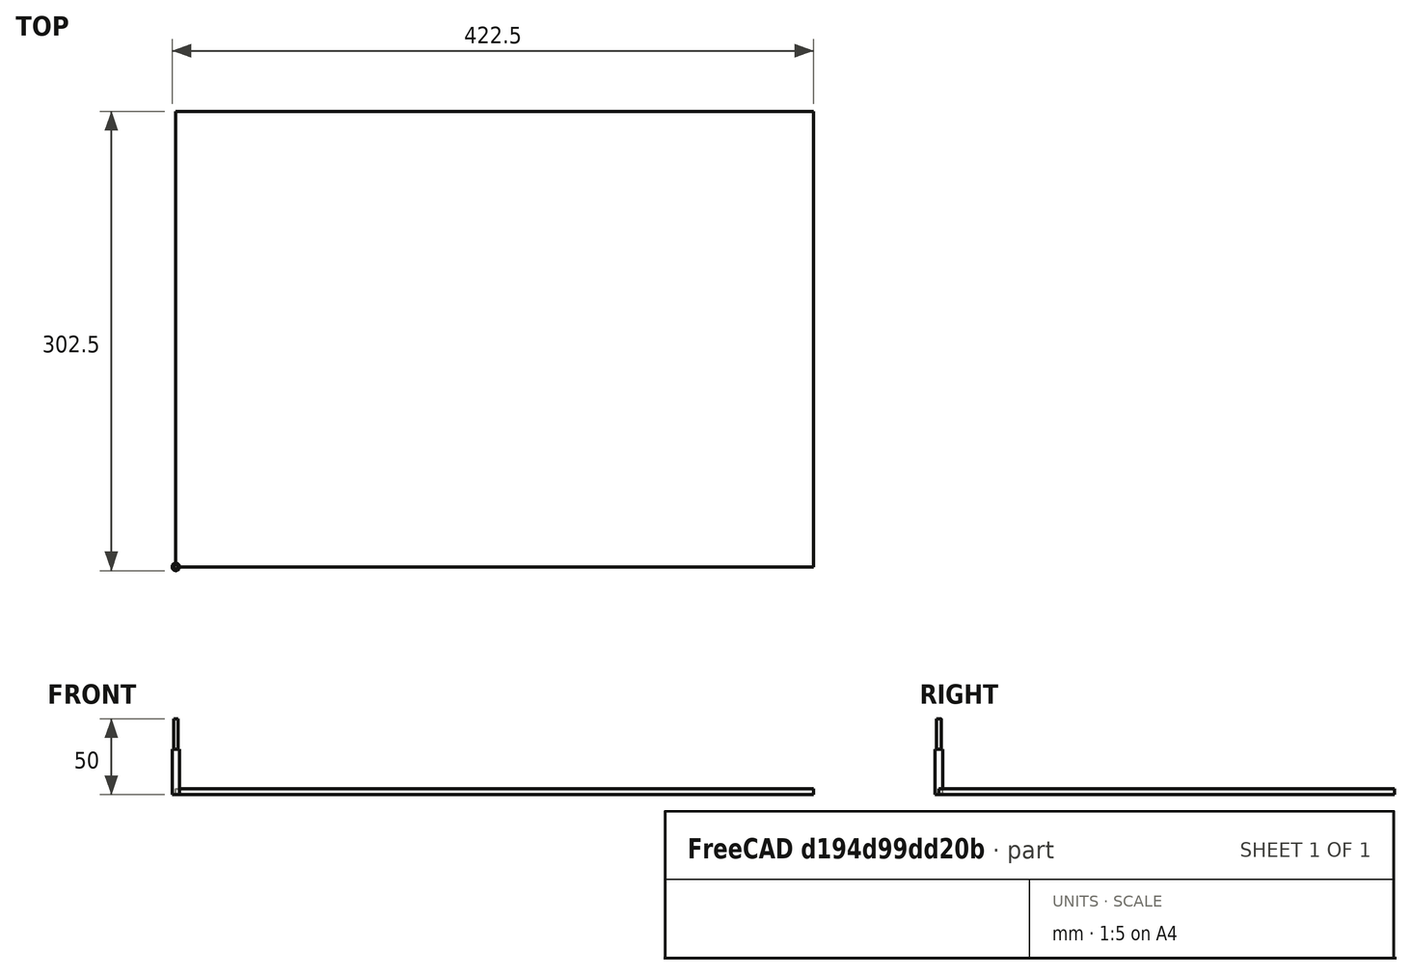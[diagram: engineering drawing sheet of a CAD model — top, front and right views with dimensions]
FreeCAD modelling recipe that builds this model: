
FCSTD DOCUMENT  (FreeCAD 0.21R33771 (Git))
Label: HousingAtari_T01
License: All rights reserved
LicenseURL: https://en.wikipedia.org/wiki/All_rights_reserved
objects: Sketcher::SketchObject×7, Part::Part2DObjectPython×5, TechDraw::DrawViewDraft×4, Path::FeaturePython×3, App::DocumentObjectGroup×3, Part::FeaturePython×2, PartDesign::Body×1, App::FeaturePython×1, Mesh::FeaturePython×1, TechDraw::DrawSVGTemplate×1, TechDraw::DrawPage×1
note: 15 computed .brp shape members not serialized (recipe doc carries the construction recipe); baked Part::Feature solids carry a one-line shape summary decoded from their .brp

FEATURE [Sketcher::SketchObject] Sketch  label="A3"
  FullyConstrained = true
  MapMode = 5
  sketch-geometry (6):
    g0: LineSegment StartX=0 StartY=0 StartZ=0 EndX=420 EndY=0 EndZ=0
    g1: LineSegment StartX=420 StartY=0 StartZ=0 EndX=420 EndY=297 EndZ=0
    g2: LineSegment StartX=0 StartY=297 StartZ=0 EndX=0 EndY=0 EndZ=0
    g3: LineSegment StartX=0 StartY=297 StartZ=0 EndX=210 EndY=297 EndZ=0
    g4: LineSegment StartX=210 StartY=297 StartZ=0 EndX=420 EndY=297 EndZ=0
    g5: LineSegment StartX=210 StartY=297 StartZ=0 EndX=210 EndY=0 EndZ=0
  constraints (16):
    c: Coincident(g0,g1)
    c: Coincident(g2,g0)
    c: Horizontal(g0)
    c: Vertical(g1)
    c: Vertical(g2)
    c: Coincident(g0,g-1)
    c: DistanceX(g2,g1) = 420
    c: DistanceY(g2,g2) = 297
    c: Coincident(g3,g2)
    c: Horizontal(g3)
    c: Coincident(g4,g3)
    c: Coincident(g4,g1)
    c: Horizontal(g4)
    c: Equal(g4,g3)
    c: Coincident(g5,g3)
    c: Symmetric(g0,g0,g5)
FEATURE [Sketcher::SketchObject] Sketch001  label="BOX-OUTLINE"
  FullyConstrained = true
  MapMode = 5
  sketch-geometry (59):
    g0: LineSegment StartX=45 StartY=255 StartZ=0 EndX=45 EndY=220 EndZ=0
    g1: LineSegment StartX=45 StartY=220 StartZ=0 EndX=45 EndY=185 EndZ=0
    g2: LineSegment StartX=45 StartY=185 StartZ=0 EndX=110 EndY=185 EndZ=0
    g3: LineSegment StartX=110 StartY=185 StartZ=0 EndX=175 EndY=185 EndZ=0
    g4: LineSegment StartX=175 StartY=185 StartZ=0 EndX=175 EndY=220 EndZ=0
    g5: LineSegment StartX=175 StartY=220 StartZ=0 EndX=175 EndY=255 EndZ=0
    g6: LineSegment StartX=175 StartY=255 StartZ=0 EndX=110 EndY=255 EndZ=0
    g7: LineSegment StartX=110 StartY=255 StartZ=0 EndX=45 EndY=255 EndZ=0
    g8: LineSegment StartX=45 StartY=185 StartZ=0 EndX=0 EndY=0 EndZ=0
    g9: LineSegment StartX=45 StartY=185 StartZ=0 EndX=45 EndY=181 EndZ=0
    g10: LineSegment StartX=45 StartY=181 StartZ=0 EndX=175 EndY=181 EndZ=0
    g11: LineSegment StartX=175 StartY=181 StartZ=0 EndX=175 EndY=185 EndZ=0
    g12: LineSegment StartX=175 StartY=185 StartZ=0 EndX=171 EndY=185 EndZ=0
    g13: LineSegment StartX=171 StartY=185 StartZ=0 EndX=171 EndY=255 EndZ=0
    g14: LineSegment StartX=171 StartY=255 StartZ=0 EndX=175 EndY=255 EndZ=0
    g15: LineSegment StartX=175 StartY=255 StartZ=0 EndX=175 EndY=259 EndZ=0
    g16: LineSegment StartX=175 StartY=259 StartZ=0 EndX=45 EndY=259 EndZ=0
    g17: LineSegment StartX=45 StartY=259 StartZ=0 EndX=45 EndY=255 EndZ=0
    g18: LineSegment StartX=45 StartY=185 StartZ=0 EndX=49 EndY=185 EndZ=0
    g19: LineSegment StartX=49 StartY=185 StartZ=0 EndX=49 EndY=255 EndZ=0
    g20: LineSegment StartX=49 StartY=255 StartZ=0 EndX=45 EndY=255 EndZ=0
    g21: LineSegment StartX=45 StartY=181 StartZ=0 EndX=45 EndY=151 EndZ=0
    g22: LineSegment StartX=45 StartY=151 StartZ=0 EndX=175 EndY=151 EndZ=0
    g23: LineSegment StartX=175 StartY=151 StartZ=0 EndX=175 EndY=181 EndZ=0
    g24: LineSegment StartX=171 StartY=185 StartZ=0 EndX=205 EndY=185 EndZ=0
    g25: LineSegment StartX=205 StartY=185 StartZ=0 EndX=205 EndY=255 EndZ=0
    g26: LineSegment StartX=205 StartY=255 StartZ=0 EndX=171 EndY=255 EndZ=0
    g27: LineSegment StartX=175 StartY=259 StartZ=0 EndX=175 EndY=289 EndZ=0
    g28: LineSegment StartX=175 StartY=289 StartZ=0 EndX=45 EndY=289 EndZ=0
    g29: LineSegment StartX=45 StartY=289 StartZ=0 EndX=45 EndY=259 EndZ=0
    g30: LineSegment StartX=49 StartY=255 StartZ=0 EndX=15 EndY=255 EndZ=0
    g31: LineSegment StartX=15 StartY=255 StartZ=0 EndX=15 EndY=185 EndZ=0
    g32: LineSegment StartX=15 StartY=185 StartZ=0 EndX=49 EndY=185 EndZ=0
    g33: LineSegment StartX=175 StartY=151 StartZ=0 EndX=171 EndY=151 EndZ=0
    g34: LineSegment StartX=171 StartY=151 StartZ=0 EndX=171 EndY=185 EndZ=0
    g35: LineSegment StartX=175 StartY=181 StartZ=0 EndX=205 EndY=181 EndZ=0
    g36: LineSegment StartX=205 StartY=181 StartZ=0 EndX=205 EndY=185 EndZ=0
    g37: LineSegment StartX=175 StartY=259 StartZ=0 EndX=205 EndY=259 EndZ=0
    g38: LineSegment StartX=205 StartY=259 StartZ=0 EndX=205 EndY=255 EndZ=0
    g39: LineSegment StartX=171 StartY=255 StartZ=0 EndX=171 EndY=289 EndZ=0
    g40: LineSegment StartX=171 StartY=289 StartZ=0 EndX=175 EndY=289 EndZ=0
    g41: LineSegment StartX=45 StartY=289 StartZ=0 EndX=49 EndY=289 EndZ=0
    g42: LineSegment StartX=49 StartY=289 StartZ=0 EndX=49 EndY=255 EndZ=0
    g43: LineSegment StartX=15 StartY=255 StartZ=0 EndX=15 EndY=259 EndZ=0
    g44: LineSegment StartX=15 StartY=259 StartZ=0 EndX=45 EndY=259 EndZ=0
    g45: LineSegment StartX=15 StartY=185 StartZ=0 EndX=15 EndY=181 EndZ=0
    g46: LineSegment StartX=15 StartY=181 StartZ=0 EndX=45 EndY=181 EndZ=0
    g47: LineSegment StartX=49 StartY=185 StartZ=0 EndX=49 EndY=151 EndZ=0
    g48: LineSegment StartX=49 StartY=151 StartZ=0 EndX=45 EndY=151 EndZ=0
    g49: LineSegment StartX=45 StartY=151 StartZ=0 EndX=45 EndY=77 EndZ=0
    g50: LineSegment StartX=45 StartY=77 StartZ=0 EndX=175 EndY=77 EndZ=0
    g51: LineSegment StartX=175 StartY=77 StartZ=0 EndX=175 EndY=151 EndZ=0
    g52: LineSegment StartX=49 StartY=151 StartZ=0 EndX=49 EndY=81 EndZ=0
    g53: LineSegment StartX=49 StartY=81 StartZ=0 EndX=171 EndY=81 EndZ=0
    g54: LineSegment StartX=171 StartY=81 StartZ=0 EndX=171 EndY=151 EndZ=0
    g55: LineSegment StartX=49 StartY=155 StartZ=0 EndX=171 EndY=155 EndZ=0
    g56: LineSegment StartX=49 StartY=81 StartZ=0 EndX=49 EndY=77 EndZ=0
    g57: LineSegment StartX=171 StartY=81 StartZ=0 EndX=171 EndY=77 EndZ=0
    g58: LineSegment StartX=49 StartY=285 StartZ=0 EndX=171 EndY=285 EndZ=0
  constraints (162):
    c: Vertical(g0)
    c: Coincident(g1,g0)
    c: Vertical(g1)
    c: Coincident(g2,g1)
    c: Horizontal(g2)
    c: Coincident(g3,g2)
    c: Horizontal(g3)
    c: Coincident(g4,g3)
    c: Vertical(g4)
    c: Coincident(g5,g4)
    c: Vertical(g5)
    c: Horizontal(g6)
    c: Coincident(g7,g6)
    c: Coincident(g7,g0)
    c: Horizontal(g7)
    c: Vertical(g2,g6)
    c: Horizontal(g0,g4)
    c: Equal(g4,g5)
    c: Equal(g7,g6)
    c: Coincident(g5,g6)
    c: DistanceY(g1,g0) = 70
    c: DistanceX(g0,g5) = 130
    c: Coincident(g8,g1)
    c: Coincident(g8,g-1)
    c: DistanceX(g8,g8) = 45
    c: DistanceY(g8,g8) = 185
    c: Coincident(g9,g1)
    c: Vertical(g9)
    c: Coincident(g10,g9)
    c: Horizontal(g10)
    c: Coincident(g11,g10)
    c: Coincident(g11,g3)
    c: Vertical(g11)
    c: Coincident(g12,g3)
    c: Horizontal(g12)
    c: Coincident(g13,g12)
    c: Vertical(g13)
    c: Coincident(g14,g13)
    c: Coincident(g14,g5)
    c: Horizontal(g14)
    c: Equal(g11,g12)
    c: DistanceY(g11,g11) = 4
    c: Coincident(g15,g5)
    c: Vertical(g15)
    c: Coincident(g16,g15)
    c: Horizontal(g16)
    c: Coincident(g17,g16)
    c: Coincident(g17,g0)
    c: Vertical(g17)
    c: Equal(g14,g15)
    c: Coincident(g18,g1)
    c: Horizontal(g18)
    c: Coincident(g19,g18)
    c: Vertical(g19)
    c: Coincident(g20,g19)
    c: Coincident(g20,g0)
    c: Horizontal(g20)
    c: Equal(g17,g20)
    c: Coincident(g21,g9)
    c: Vertical(g21)
    c: Coincident(g22,g21)
    c: Horizontal(g22)
    c: Coincident(g23,g22)
    c: Coincident(g23,g10)
    c: Coincident(g24,g12)
    c: Horizontal(g24)
    c: Coincident(g25,g24)
    c: Vertical(g25)
    c: Coincident(g26,g25)
    c: Coincident(g26,g13)
    c: Horizontal(g26)
    c: Coincident(g27,g15)
    c: Vertical(g27)
    c: Coincident(g28,g27)
    c: Horizontal(g28)
    c: Coincident(g29,g28)
    c: Coincident(g29,g16)
    c: Coincident(g30,g19)
    c: Horizontal(g30)
    c: Coincident(g31,g30)
    c: Vertical(g31)
    c: Coincident(g32,g31)
    c: Coincident(g32,g18)
    c: Horizontal(g32)
    c: Vertical(g23)
    c: Coincident(g33,g22)
    c: Horizontal(g33)
    c: Coincident(g34,g33)
    c: Coincident(g34,g12)
    c: Vertical(g34)
    c: Coincident(g35,g10)
    c: Horizontal(g35)
    c: Coincident(g36,g35)
    c: Coincident(g36,g24)
    c: Coincident(g37,g15)
    c: Horizontal(g37)
    c: Coincident(g38,g37)
    c: Coincident(g38,g25)
    c: Coincident(g39,g13)
    c: Vertical(g39)
    c: Coincident(g40,g39)
    c: Coincident(g40,g27)
    c: Horizontal(g40)
    c: Coincident(g41,g28)
    c: Horizontal(g41)
    c: Coincident(g42,g41)
    c: Coincident(g42,g19)
    c: Coincident(g43,g30)
    c: Vertical(g43)
    c: Coincident(g44,g43)
    c: Coincident(g44,g16)
    c: Coincident(g45,g31)
    c: Vertical(g45)
    c: Coincident(g46,g45)
    c: Coincident(g46,g9)
    c: Horizontal(g46)
    c: Coincident(g47,g18)
    c: Coincident(g48,g47)
    c: Coincident(g48,g21)
    c: Vertical(g38)
    c: Vertical(g47)
    c: Vertical(g36)
    c: Horizontal(g44)
    c: Horizontal(g48)
    c: DistanceY(g16,g28) = 30
    c: Vertical(g42)
    c: Vertical(g29)
    c: DistanceY(g23,g23) = 30
    c: Distance(g44,g44) = 30
    c: DistanceX(g35,g35) = 30
    c: Coincident(g49,g21)
    c: Vertical(g49)
    c: Coincident(g50,g49)
    c: Horizontal(g50)
    c: Coincident(g51,g50)
    c: Coincident(g51,g22)
    c: Vertical(g51)
    c: Coincident(g52,g47)
    c: Vertical(g52)
    c: Coincident(g53,g52)
    c: Horizontal(g53)
    c: Coincident(g54,g53)
    c: Coincident(g54,g33)
    c: Vertical(g54)
    c: PointOnObject(g55,g47)
    c: PointOnObject(g55,g34)
    c: Horizontal(g55)
    c: DistanceY(g47,g55) = 4
    c: Coincident(g56,g52)
    c: PointOnObject(g56,g50)
    c: Vertical(g56)
    c: DistanceY(g56,g56) = 4
    c: DistanceY(g52,g52) = 70
    c: DistanceY(g35,g37) = 78
    c: Coincident(g57,g53)
    c: PointOnObject(g57,g50)
    c: Vertical(g57)
    c: DistanceY(g57,g55) = 78
    c: PointOnObject(g58,g42)
    c: PointOnObject(g58,g39)
    c: Horizontal(g58)
    c: DistanceY(g58,g39) = 4
FEATURE [PartDesign::Body] Body
  Group = -> [Sketch,Sketch001]
  Origin = -> Origin
FEATURE [Sketcher::SketchObject] Sketch002  label="CUT-BOX-BASE"
  ExternalGeometry = -> [Sketch001]
  FullyConstrained = false
  MapMode = 5
  sketch-geometry (30):
    g0: LineSegment StartX=45 StartY=220 StartZ=0 EndX=175 EndY=220 EndZ=0
    g1: LineSegment StartX=110 StartY=185 StartZ=0 EndX=110 EndY=255 EndZ=0
    g2: LineSegment StartX=49 StartY=205 StartZ=0 EndX=171 EndY=205 EndZ=0
    g3: LineSegment StartX=49 StartY=235 StartZ=0 EndX=171 EndY=235 EndZ=0
    g4: LineSegment StartX=83.7703 StartY=185 StartZ=0 EndX=83.7703 EndY=255 EndZ=0
    g5: LineSegment StartX=133.77 StartY=185 StartZ=0 EndX=133.77 EndY=255 EndZ=0
    g6: LineSegment StartX=49 StartY=205 StartZ=0 EndX=49 EndY=220 EndZ=0
    g7: LineSegment StartX=49 StartY=220 StartZ=0 EndX=49 EndY=235 EndZ=0
    g8: LineSegment StartX=171 StartY=205 StartZ=0 EndX=171 EndY=220 EndZ=0
    g9: LineSegment StartX=171 StartY=220 StartZ=0 EndX=171 EndY=235 EndZ=0
    g10: LineSegment StartX=171 StartY=205 StartZ=0 EndX=175 EndY=205 EndZ=0
    g11: LineSegment StartX=171 StartY=235 StartZ=0 EndX=175 EndY=235 EndZ=0
    g12: LineSegment StartX=49 StartY=235 StartZ=0 EndX=45 EndY=235 EndZ=0
    g13: LineSegment StartX=49 StartY=205 StartZ=0 EndX=45 EndY=205 EndZ=0
    g14: LineSegment StartX=83.7703 StartY=185 StartZ=0 EndX=110 EndY=185 EndZ=0
    g15: LineSegment StartX=110 StartY=185 StartZ=0 EndX=133.77 EndY=185 EndZ=0
    g16: LineSegment StartX=83.7703 StartY=185 StartZ=0 EndX=83.7703 EndY=181 EndZ=0
    g17: LineSegment StartX=133.77 StartY=185 StartZ=0 EndX=133.77 EndY=181 EndZ=0
    g18: LineSegment StartX=83.7703 StartY=255 StartZ=0 EndX=110 EndY=255 EndZ=0
    g19: LineSegment StartX=110 StartY=255 StartZ=0 EndX=133.77 EndY=255 EndZ=0
    g20: LineSegment StartX=133.77 StartY=255 StartZ=0 EndX=133.77 EndY=259 EndZ=0
    g21: LineSegment StartX=83.7703 StartY=255 StartZ=0 EndX=83.7703 EndY=259 EndZ=0
    g22: LineSegment StartX=45 StartY=205 StartZ=0 EndX=45 EndY=181 EndZ=0
    g23: LineSegment StartX=45 StartY=181 StartZ=0 EndX=83.7703 EndY=181 EndZ=0
    g24: LineSegment StartX=133.77 StartY=181 StartZ=0 EndX=175 EndY=181 EndZ=0
    g25: LineSegment StartX=175 StartY=181 StartZ=0 EndX=175 EndY=205 EndZ=0
    g26: LineSegment StartX=175 StartY=235 StartZ=0 EndX=175 EndY=259 EndZ=0
    g27: LineSegment StartX=175 StartY=259 StartZ=0 EndX=133.77 EndY=259 EndZ=0
    g28: LineSegment StartX=83.7703 StartY=259 StartZ=0 EndX=45 EndY=259 EndZ=0
    g29: LineSegment StartX=45 StartY=259 StartZ=0 EndX=45 EndY=235 EndZ=0
  constraints (75):
    c: Coincident(g0,g-4)
    c: Coincident(g0,g-6)
    c: Coincident(g1,g-10)
    c: PointOnObject(g3,g-11)
    c: PointOnObject(g4,g-10)
    c: PointOnObject(g2,g-9)
    c: PointOnObject(g3,g-9)
    c: Horizontal(g2)
    c: Vertical(g4)
    c: Vertical(g5)
    c: Horizontal(g3)
    c: PointOnObject(g2,g-11)
    c: PointOnObject(g5,g-13)
    c: Coincident(g1,g-13)
    c: PointOnObject(g4,g-12)
    c: Coincident(g6,g2)
    c: Symmetric(g-11,g-11,g6)
    c: Coincident(g7,g6)
    c: Coincident(g7,g3)
    c: Equal(g6,g7)
    c: DistanceY(g2,g3) = 30
    c: DistanceX(g4,g5) = 50
    c: Coincident(g8,g2)
    c: Symmetric(g-9,g-9,g8)
    c: Coincident(g9,g8)
    c: Coincident(g9,g3)
    c: Coincident(g10,g2)
    c: PointOnObject(g10,g-6)
    c: Horizontal(g10)
    c: Coincident(g11,g3)
    c: PointOnObject(g11,g-5)
    c: Horizontal(g11)
    c: Coincident(g12,g3)
    c: PointOnObject(g12,g-4)
    c: Horizontal(g12)
    c: Coincident(g13,g2)
    c: PointOnObject(g13,g-3)
    c: Horizontal(g13)
    c: Coincident(g14,g4)
    c: Coincident(g14,g1)
    c: Coincident(g15,g1)
    c: Coincident(g15,g5)
    c: Horizontal(g15)
    c: Coincident(g16,g4)
    c: PointOnObject(g16,g-7)
    c: Vertical(g16)
    c: Coincident(g17,g5)
    c: PointOnObject(g17,g-7)
    c: Vertical(g17)
    c: Coincident(g18,g4)
    c: Coincident(g18,g1)
    c: Coincident(g19,g1)
    c: Coincident(g19,g5)
    c: Coincident(g20,g5)
    c: PointOnObject(g20,g-14)
    c: Vertical(g20)
    c: Coincident(g21,g4)
    c: PointOnObject(g21,g-14)
    c: Vertical(g21)
    c: Coincident(g22,g13)
    c: Coincident(g22,g-7)
    c: Coincident(g23,g22)
    c: Coincident(g23,g16)
    c: Coincident(g24,g17)
    c: Coincident(g24,g-7)
    c: Coincident(g25,g24)
    c: Coincident(g25,g10)
    c: Coincident(g26,g11)
    c: Coincident(g26,g-14)
    c: Coincident(g27,g26)
    c: Coincident(g27,g20)
    c: Coincident(g28,g21)
    c: Coincident(g28,g-14)
    c: Coincident(g29,g28)
    c: Coincident(g29,g12)
FEATURE [App::FeaturePython] SetupSheet  # Path/CAM operation (typed FeaturePython)
  ClearanceHeightExpression = OpStockZMax+SetupSheet.ClearanceHeightOffset
  ClearanceHeightOffset = 5
  CoolantMode = 0
  CoolantModes = None | Flood | Mist
  FinalDepthExpression = OpFinalDepth
  HorizRapid = 0
  SafeHeightExpression = OpStockZMax+SetupSheet.SafeHeightOffset
  SafeHeightOffset = 3
  StartDepthExpression = OpStartDepth
  StepDownExpression = OpToolDiameter
  VertRapid = 0
FEATURE [Part::Part2DObjectPython] Clone2D  label="Model-CUT-BOX"  # Draft 2D object (typed FeaturePython)
  Fuse = false
  Objects = -> [Sketch002]
  PathResource = Model
  Scale = (1,1,1)
FEATURE [Part::FeaturePython] ToolBit  label="Endmill"  # Path/CAM toolbit (typed FeaturePython)
  BitPropertyNames = Chipload | CuttingEdgeHeight | Diameter | Flutes | Length | Material | ShankDiameter | SpindleDirection
  BitShape = <path>
  Chipload = 0
  CuttingEdgeHeight = 30
  Diameter = 5
  Flutes = 0
  Length = 50
  Material = 0
  ShankDiameter = 3
  ShapeName = endmill
  SpindleDirection = 0
FEATURE [Path::FeaturePython] TC__Default_Tool  label="TC: Default Tool"  # Path/CAM operation (typed FeaturePython)
  HorizFeed = 1000
  HorizRapid = 1000
  SpindleDir = 0
  SpindleSpeed = 1000
  Tool = -> ToolBit
  ToolNumber = 1
  VertFeed = 1000
  VertRapid = 1000
  expr: HorizRapid = 1000
  expr: VertRapid = 1000
FEATURE [App::DocumentObjectGroup] Tools
  Group = -> [TC__Default_Tool]
FEATURE [Path::FeaturePython] Engrave  # Path/CAM operation (typed FeaturePython)
  Active = true
  ClearanceHeight = 9
  CoolantMode = 0
  CycleTime = 00:00:03
  FinalDepth = -5
  OpFinalDepth = -5
  OpStartDepth = 0
  OpStockZMax = 4
  OpStockZMin = 0
  OpToolDiameter = 5
  SafeHeight = 7
  StartDepth = 0
  StartVertex = 0
  StepDown = 5
  ToolController = -> TC__Default_Tool
  expr: ClearanceHeight = OpStockZMax + SetupSheet.ClearanceHeightOffset
  expr: FinalDepth = OpFinalDepth
  expr: SafeHeight = OpStockZMax + SetupSheet.SafeHeightOffset
  expr: StartDepth = OpStartDepth
  expr: StepDown = OpToolDiameter
FEATURE [App::DocumentObjectGroup] Operations
  Group = -> [Engrave]
FEATURE [Part::FeaturePython] Stock001  # WARN: FeaturePython — macro-defined, semantics opaque (R4)
  Height = 4
  Length = 420
  StockType = CreateBox
  Width = 300
FEATURE [Mesh::FeaturePython] CutMaterial  # WARN: FeaturePython — macro-defined, semantics opaque (R4)
FEATURE [Sketcher::SketchObject] Sketch004  label="CUT-BOX-WALLS"
  ExternalGeometry = -> [Sketch002,Sketch001]
  FullyConstrained = false
  MapMode = 5
  sketch-geometry (32):
    g0: LineSegment StartX=45 StartY=259 StartZ=0 EndX=30 EndY=259 EndZ=0
    g1: LineSegment StartX=30 StartY=259 StartZ=0 EndX=30 EndY=255 EndZ=0
    g2: LineSegment StartX=30 StartY=255 StartZ=0 EndX=15 EndY=255 EndZ=0
    g3: LineSegment StartX=15 StartY=185 StartZ=0 EndX=30 EndY=185 EndZ=0
    g4: LineSegment StartX=30 StartY=185 StartZ=0 EndX=30 EndY=181 EndZ=0
    g5: LineSegment StartX=30 StartY=181 StartZ=0 EndX=45 EndY=181 EndZ=0
    g6: LineSegment StartX=175 StartY=181 StartZ=0 EndX=190 EndY=181 EndZ=0
    g7: LineSegment StartX=190 StartY=181 StartZ=0 EndX=190 EndY=185 EndZ=0
    g8: LineSegment StartX=190 StartY=185 StartZ=0 EndX=205 EndY=185 EndZ=0
    g9: LineSegment StartX=205 StartY=255 StartZ=0 EndX=190 EndY=255 EndZ=0
    g10: LineSegment StartX=190 StartY=255 StartZ=0 EndX=190 EndY=259 EndZ=0
    g11: LineSegment StartX=190 StartY=259 StartZ=0 EndX=175 EndY=259 EndZ=0
    g12: LineSegment StartX=30 StartY=185 StartZ=0 EndX=30 EndY=255 EndZ=0
    g13: LineSegment StartX=190 StartY=185 StartZ=0 EndX=190 EndY=255 EndZ=0
    g14: LineSegment StartX=15 StartY=220 StartZ=0 EndX=205 EndY=220 EndZ=0
    g15: LineSegment StartX=110 StartY=151 StartZ=0 EndX=110 EndY=289 EndZ=0
    g16: LineSegment StartX=15 StartY=255 StartZ=0 EndX=15 EndY=235 EndZ=0
    g17: LineSegment StartX=15 StartY=235 StartZ=0 EndX=20.6579 EndY=235 EndZ=0
    g18: LineSegment StartX=20.6579 StartY=235 StartZ=0 EndX=20.6579 EndY=205 EndZ=0
    g19: LineSegment StartX=20.6579 StartY=204.687 StartZ=0 EndX=15 EndY=204.687 EndZ=0
    g20: LineSegment StartX=15 StartY=204.687 StartZ=0 EndX=15 EndY=185 EndZ=0
    g21: LineSegment StartX=205 StartY=185 StartZ=0 EndX=205 EndY=205 EndZ=0
    g22: LineSegment StartX=205 StartY=205 StartZ=0 EndX=199.009 EndY=205 EndZ=0
    g23: LineSegment StartX=199.009 StartY=205 StartZ=0 EndX=199.009 EndY=235 EndZ=0
    g24: LineSegment StartX=199.009 StartY=235 StartZ=0 EndX=205 EndY=235 EndZ=0
    g25: LineSegment StartX=205 StartY=235 StartZ=0 EndX=205 EndY=255 EndZ=0
    g26: LineSegment StartX=20.6579 StartY=235 StartZ=0 EndX=45 EndY=235 EndZ=0
    g27: LineSegment StartX=49 StartY=235 StartZ=0 EndX=170.368 EndY=235 EndZ=0
    g28: LineSegment StartX=175 StartY=235 StartZ=0 EndX=199.009 EndY=235 EndZ=0
    g29: LineSegment StartX=22.3684 StartY=205 StartZ=0 EndX=45 EndY=205 EndZ=0
    g30: LineSegment StartX=49.8267 StartY=205 StartZ=0 EndX=171 EndY=205 EndZ=0
    g31: LineSegment StartX=175 StartY=205 StartZ=0 EndX=199.009 EndY=205 EndZ=0
  constraints (82):
    c: Coincident(g0,g-18)
    c: Horizontal(g0)
    c: Coincident(g1,g0)
    c: Vertical(g1)
    c: Coincident(g2,g1)
    c: Coincident(g2,g-20)
    c: Horizontal(g2)
    c: Horizontal(g3)
    c: Coincident(g4,g3)
    c: Vertical(g4)
    c: Coincident(g5,g4)
    c: Coincident(g5,g-7)
    c: Horizontal(g5)
    c: Coincident(g6,g-11)
    c: Horizontal(g6)
    c: Coincident(g7,g6)
    c: Vertical(g7)
    c: Coincident(g8,g7)
    c: Coincident(g8,g-21)
    c: Horizontal(g8)
    c: Horizontal(g9)
    c: Coincident(g10,g9)
    c: Vertical(g10)
    c: Coincident(g11,g10)
    c: Coincident(g11,g-15)
    c: Horizontal(g11)
    c: Coincident(g12,g3)
    c: Coincident(g12,g1)
    c: Vertical(g12)
    c: Coincident(g13,g7)
    c: Coincident(g13,g9)
    c: Vertical(g13)
    c: Equal(g2,g0)
    c: Equal(g9,g11)
    c: DistanceX(g2,g2) = 15
    c: Distance(g9,g9) = 15
    c: PointOnObject(g14,g-20)
    c: PointOnObject(g14,g-21)
    c: Horizontal(g14)
    c: Symmetric(g-22,g-22,g15)
    c: Symmetric(g-19,g-19,g15)
    c: PointOnObject(g-13,g14)
    c: Coincident(g16,g2)
    c: PointOnObject(g16,g-20)
    c: Coincident(g17,g16)
    c: Horizontal(g17)
    c: Coincident(g18,g17)
    c: Vertical(g18)
    c: PointOnObject(g19,g-20)
    c: Horizontal(g19)
    c: Coincident(g20,g19)
    c: Coincident(g20,g3)
    c: Vertical(g20)
    c: Coincident(g21,g8)
    c: PointOnObject(g21,g-21)
    c: Coincident(g22,g21)
    c: Horizontal(g22)
    c: Coincident(g23,g22)
    c: Vertical(g23)
    c: Coincident(g24,g23)
    c: PointOnObject(g24,g-21)
    c: Horizontal(g24)
    c: PointOnObject(g25,g-21)
    c: Coincident(g25,g9)
    c: Vertical(g25)
    c: Horizontal(g17,g-3)
    c: Horizontal(g18,g-6)
    c: Horizontal(g-11,g22)
    c: Horizontal(g-14,g23)
    c: Coincident(g26,g17)
    c: Coincident(g26,g-3)
    c: Coincident(g27,g-4)
    c: Horizontal(g27)
    c: Coincident(g28,g-14)
    c: Coincident(g28,g23)
    c: Coincident(g29,g-6)
    c: Horizontal(g29)
    c: Coincident(g30,g-12)
    c: Horizontal(g30)
    c: Coincident(g31,g-11)
    c: Coincident(g31,g22)
    c: PointOnObject(g25,g24)
FEATURE [Sketcher::SketchObject] Sketch005  label="CUT-BOX-WALS2"
  ExternalGeometry = -> [Sketch002,Sketch001]
  FullyConstrained = true
  MapMode = 5
  sketch-geometry (28):
    g0: LineSegment StartX=83.7703 StartY=181 StartZ=0 EndX=83.7703 EndY=151 EndZ=0
    g1: LineSegment StartX=133.77 StartY=181 StartZ=0 EndX=133.77 EndY=151 EndZ=0
    g2: LineSegment StartX=83.7703 StartY=151 StartZ=0 EndX=83.7703 EndY=155 EndZ=0
    g3: LineSegment StartX=83.7703 StartY=155 StartZ=0 EndX=133.77 EndY=155 EndZ=0
    g4: LineSegment StartX=133.77 StartY=155 StartZ=0 EndX=133.77 EndY=151 EndZ=0
    g5: LineSegment StartX=83.7703 StartY=259 StartZ=0 EndX=83.7703 EndY=289 EndZ=0
    g6: LineSegment StartX=133.77 StartY=259 StartZ=0 EndX=133.77 EndY=289 EndZ=0
    g7: LineSegment StartX=49 StartY=166 StartZ=0 EndX=171 EndY=166 EndZ=0
    g8: LineSegment StartX=45 StartY=166 StartZ=0 EndX=49 EndY=166 EndZ=0
    g9: LineSegment StartX=175 StartY=166 StartZ=0 EndX=171 EndY=166 EndZ=0
    g10: LineSegment StartX=175 StartY=274 StartZ=0 EndX=45 EndY=274 EndZ=0
    g11: LineSegment StartX=45 StartY=274 StartZ=0 EndX=49 EndY=274 EndZ=0
    g12: LineSegment StartX=175 StartY=274 StartZ=0 EndX=171 EndY=274 EndZ=0
    g13: LineSegment StartX=83.7703 StartY=289 StartZ=0 EndX=83.7703 EndY=285 EndZ=0
    g14: LineSegment StartX=83.7703 StartY=285 StartZ=0 EndX=133.77 EndY=285 EndZ=0
    g15: LineSegment StartX=133.77 StartY=285 StartZ=0 EndX=133.77 EndY=289 EndZ=0
    g16: LineSegment StartX=49 StartY=181 StartZ=0 EndX=49 EndY=166 EndZ=0
    g17: LineSegment StartX=45 StartY=166 StartZ=0 EndX=45 EndY=151 EndZ=0
    g18: LineSegment StartX=45 StartY=151 StartZ=0 EndX=83.7703 EndY=151 EndZ=0
    g19: LineSegment StartX=133.77 StartY=151 StartZ=0 EndX=175 EndY=151 EndZ=0
    g20: LineSegment StartX=175 StartY=151 StartZ=0 EndX=175 EndY=166 EndZ=0
    g21: LineSegment StartX=171 StartY=166 StartZ=0 EndX=171 EndY=181 EndZ=0
    g22: LineSegment StartX=49 StartY=259 StartZ=0 EndX=49 EndY=274 EndZ=0
    g23: LineSegment StartX=45 StartY=274 StartZ=0 EndX=45 EndY=289 EndZ=0
    g24: LineSegment StartX=45 StartY=289 StartZ=0 EndX=83.7703 EndY=289 EndZ=0
    g25: LineSegment StartX=133.77 StartY=289 StartZ=0 EndX=175 EndY=289 EndZ=0
    g26: LineSegment StartX=175 StartY=289 StartZ=0 EndX=175 EndY=274 EndZ=0
    g27: LineSegment StartX=171 StartY=274 StartZ=0 EndX=171 EndY=259 EndZ=0
  constraints (75):
    c: PointOnObject(g7,g-11)
    c: Coincident(g0,g-4)
    c: PointOnObject(g0,g-9)
    c: Vertical(g0)
    c: Coincident(g1,g-3)
    c: PointOnObject(g1,g-9)
    c: Vertical(g1)
    c: Coincident(g2,g0)
    c: PointOnObject(g2,g-10)
    c: Vertical(g2)
    c: Coincident(g3,g2)
    c: PointOnObject(g3,g-10)
    c: Coincident(g4,g3)
    c: Coincident(g4,g1)
    c: Vertical(g4)
    c: Coincident(g5,g-5)
    c: PointOnObject(g5,g-17)
    c: Vertical(g5)
    c: Coincident(g6,g-6)
    c: Vertical(g6)
    c: Horizontal(g7)
    c: PointOnObject(g7,g-8)
    c: PointOnObject(g8,g-7)
    c: Coincident(g8,g7)
    c: Horizontal(g8)
    c: Coincident(g9,g7)
    c: Horizontal(g9)
    c: Symmetric(g-13,g-13,g10)
    c: Symmetric(g-16,g-16,g10)
    c: Coincident(g11,g10)
    c: PointOnObject(g11,g10)
    c: Coincident(g12,g10)
    c: PointOnObject(g12,g10)
    c: PointOnObject(g6,g-17)
    c: Coincident(g13,g5)
    c: PointOnObject(g13,g5)
    c: Coincident(g14,g13)
    c: PointOnObject(g14,g6)
    c: Horizontal(g14)
    c: Coincident(g15,g14)
    c: Coincident(g15,g6)
    c: PointOnObject(g14,g-24)
    c: DistanceY(g9,g-20) = 15
    c: DistanceY(g-18,g10) = 15
    c: PointOnObject(g16,g-20)
    c: Coincident(g16,g7)
    c: Vertical(g16)
    c: Coincident(g17,g8)
    c: Coincident(g17,g-9)
    c: Coincident(g18,g17)
    c: Coincident(g18,g0)
    c: Coincident(g19,g1)
    c: Coincident(g19,g-12)
    c: Coincident(g20,g19)
    c: Coincident(g20,g9)
    c: Vertical(g20)
    c: Coincident(g21,g7)
    c: PointOnObject(g21,g-20)
    c: Vertical(g21)
    c: PointOnObject(g22,g-18)
    c: Coincident(g22,g11)
    c: Vertical(g22)
    c: Coincident(g23,g10)
    c: Coincident(g23,g-17)
    c: Coincident(g24,g23)
    c: Coincident(g24,g5)
    c: Coincident(g25,g6)
    c: Coincident(g25,g-17)
    c: Coincident(g26,g25)
    c: Coincident(g26,g10)
    c: Coincident(g27,g12)
    c: PointOnObject(g27,g-18)
    c: Vertical(g27)
    c: PointOnObject(g11,g-15)
    c: PointOnObject(g12,g-14)
FEATURE [Sketcher::SketchObject] Sketch006  label="CUT-ROOF"
  ExternalGeometry = -> [Sketch005,Sketch004,Sketch001]
  FullyConstrained = false
  MapMode = 2
  sketch-geometry (22):
    g0: LineSegment StartX=218.305 StartY=259 StartZ=0 EndX=218.305 EndY=181 EndZ=0
    g1: LineSegment StartX=190 StartY=181 StartZ=0 EndX=218.305 EndY=181 EndZ=0
    g2: LineSegment StartX=190 StartY=259 StartZ=0 EndX=218.305 EndY=259 EndZ=0
    g3: LineSegment StartX=49 StartY=151 StartZ=0 EndX=49 EndY=131 EndZ=0
    g4: LineSegment StartX=83.7703 StartY=151 StartZ=0 EndX=83.7703 EndY=77 EndZ=0
    g5: LineSegment StartX=133.77 StartY=151 StartZ=0 EndX=133.77 EndY=77 EndZ=0
    g6: LineSegment StartX=49 StartY=131 StartZ=0 EndX=171 EndY=131 EndZ=0
    g7: LineSegment StartX=49 StartY=101 StartZ=0 EndX=171 EndY=101 EndZ=0
    g8: LineSegment StartX=49 StartY=131 StartZ=0 EndX=45 EndY=131 EndZ=0
    g9: LineSegment StartX=45 StartY=131 StartZ=0 EndX=45 EndY=101 EndZ=0
    g10: LineSegment StartX=45 StartY=101 StartZ=0 EndX=49 EndY=101 EndZ=0
    g11: LineSegment StartX=49 StartY=101 StartZ=0 EndX=49 EndY=81 EndZ=0
    g12: LineSegment StartX=49 StartY=81 StartZ=0 EndX=83.7703 EndY=81 EndZ=0
    g13: LineSegment StartX=83.7703 StartY=81 StartZ=0 EndX=83.7703 EndY=77 EndZ=0
    g14: LineSegment StartX=83.7703 StartY=77 StartZ=0 EndX=133.77 EndY=77 EndZ=0
    g15: LineSegment StartX=133.77 StartY=77 StartZ=0 EndX=133.77 EndY=81 EndZ=0
    g16: LineSegment StartX=133.77 StartY=81 StartZ=0 EndX=171 EndY=81 EndZ=0
    g17: LineSegment StartX=171 StartY=81 StartZ=0 EndX=171 EndY=101 EndZ=0
    g18: LineSegment StartX=171 StartY=101 StartZ=0 EndX=175 EndY=101 EndZ=0
    g19: LineSegment StartX=175 StartY=101 StartZ=0 EndX=175 EndY=131 EndZ=0
    g20: LineSegment StartX=175 StartY=131 StartZ=0 EndX=171 EndY=131 EndZ=0
    g21: LineSegment StartX=171 StartY=131 StartZ=0 EndX=171 EndY=151 EndZ=0
  constraints (61):
    c: Vertical(g0)
    c: Coincident(g1,g-9)
    c: Coincident(g1,g0)
    c: Coincident(g2,g-8)
    c: Coincident(g2,g0)
    c: Horizontal(g2)
    c: Horizontal(g1)
    c: DistanceY(g0,g0) = 78
    c: Coincident(g3,g-10)
    c: PointOnObject(g3,g-10)
    c: Coincident(g4,g-3)
    c: PointOnObject(g4,g-12)
    c: Vertical(g4)
    c: Coincident(g5,g-5)
    c: PointOnObject(g5,g-12)
    c: Vertical(g5)
    c: Coincident(g6,g3)
    c: PointOnObject(g6,g-14)
    c: Horizontal(g6)
    c: PointOnObject(g7,g-10)
    c: PointOnObject(g7,g-14)
    c: Horizontal(g7)
    c: Coincident(g8,g3)
    c: PointOnObject(g8,g-11)
    c: Coincident(g9,g8)
    c: PointOnObject(g9,g-11)
    c: Coincident(g10,g9)
    c: Coincident(g10,g7)
    c: Coincident(g11,g7)
    c: Coincident(g11,g-13)
    c: Coincident(g12,g11)
    c: PointOnObject(g12,g4)
    c: Horizontal(g12)
    c: Coincident(g13,g12)
    c: Coincident(g13,g4)
    c: Coincident(g14,g4)
    c: Coincident(g14,g5)
    c: Coincident(g15,g5)
    c: PointOnObject(g15,g-13)
    c: Vertical(g15)
    c: Coincident(g16,g15)
    c: Coincident(g16,g-14)
    c: Coincident(g17,g16)
    c: Coincident(g17,g7)
    c: Coincident(g18,g7)
    c: PointOnObject(g18,g-15)
    c: Horizontal(g18)
    c: Coincident(g19,g18)
    c: PointOnObject(g19,g-15)
    c: Coincident(g20,g19)
    c: Coincident(g20,g6)
    c: Coincident(g21,g6)
    c: Coincident(g21,g-14)
    c: Horizontal(g20)
    c: Horizontal(g8)
    c: DistanceY(g21,g21) = 20
    c: DistanceY(g17,g17) = 20
    c: Horizontal(g10)
    c: DistanceY(g-17,g-17) = 30
    c: Distance(g19,g19) = 30
    c: DistanceY(g11,g3) = 70
FEATURE [Sketcher::SketchObject] Sketch003  label="CUT-Functional"
  ExternalGeometry = -> [Sketch006,Sketch002]
  FullyConstrained = false
  MapMode = 5
  sketch-geometry (71):
    g0: LineSegment StartX=187.965 StartY=207.959 StartZ=0 EndX=187.965 EndY=232.959 EndZ=0
    g1: Circle CenterX=187.965 CenterY=207.959 CenterZ=0 NormalX=0 NormalY=0 NormalZ=1 AngleXU=0 Radius=2
    g2: Circle CenterX=187.965 CenterY=232.959 CenterZ=0 NormalX=0 NormalY=0 NormalZ=1 AngleXU=0 Radius=2
    g3: LineSegment StartX=184.184 StartY=228.22 StartZ=0 EndX=187.971 EndY=229.624 EndZ=0
    g4: LineSegment StartX=187.971 StartY=229.624 StartZ=0 EndX=191.35 EndY=230.87 EndZ=0
    g5: LineSegment StartX=192.965 StartY=229.865 StartZ=0 EndX=192.965 EndY=220.459 EndZ=0
    g6: LineSegment StartX=192.965 StartY=220.459 StartZ=0 EndX=192.965 EndY=211.298 EndZ=0
    g7: LineSegment StartX=191.339 StartY=210.051 StartZ=0 EndX=187.965 EndY=211.279 EndZ=0
    g8: LineSegment StartX=187.965 StartY=211.279 StartZ=0 EndX=184.188 EndY=212.653 EndZ=0
    g9: LineSegment StartX=182.965 StartY=214.563 StartZ=0 EndX=182.966 EndY=220.459 EndZ=0
    g10: LineSegment StartX=182.966 StartY=220.459 StartZ=0 EndX=182.997 EndY=226.439 EndZ=0
    g11: LineSegment StartX=182.966 StartY=220.459 StartZ=0 EndX=187.965 EndY=220.459 EndZ=0
    g12: LineSegment StartX=187.965 StartY=220.459 StartZ=0 EndX=192.965 EndY=220.459 EndZ=0
    g13: ArcOfCircle CenterX=192.05 CenterY=210.766 CenterZ=0 NormalX=0 NormalY=0 NormalZ=1 AngleXU=0 Radius=0.915581 StartAngle=4.36332 EndAngle=6.28319
    g14: GeomPoint X=192.965 Y=209.459 Z=0
    g15: LineSegment StartX=192.083 StartY=210.149 StartZ=0 EndX=192.529 EndY=210.461 EndZ=0
    g16: ArcOfCircle CenterX=192.05 CenterY=230.151 CenterZ=0 NormalX=0 NormalY=0 NormalZ=1 AngleXU=0 Radius=0.915581 StartAngle=-1.51e-14 EndAngle=1.91986
    g17: GeomPoint X=192.965 Y=231.459 Z=0
    g18: LineSegment StartX=192.73 StartY=230.316 StartZ=0 EndX=192.073 EndY=230.776 EndZ=0
    g19: ArcOfCircle CenterX=184.273 CenterY=226.903 CenterZ=0 NormalX=0 NormalY=0 NormalZ=1 AngleXU=0 Radius=1.30759 StartAngle=1.91986 EndAngle=3.14159
    g20: GeomPoint X=182.965 Y=227.819 Z=0
    g21: LineSegment StartX=183.586 StartY=227.75 StartZ=0 EndX=183.246 EndY=227.247 EndZ=0
    g22: ArcOfCircle CenterX=184.273 CenterY=214.014 CenterZ=0 NormalX=0 NormalY=0 NormalZ=1 AngleXU=0 Radius=1.30759 StartAngle=3.14159 EndAngle=4.36332
    g23: GeomPoint X=182.965 Y=213.098 Z=0
    g24: LineSegment StartX=183.28 StartY=213.564 StartZ=0 EndX=183.604 EndY=213.101 EndZ=0
    g25: LineSegment StartX=27.8518 StartY=233.284 StartZ=0 EndX=27.8518 EndY=206.716 EndZ=0
    g26: LineSegment StartX=29.5678 StartY=205 StartZ=0 EndX=36.1358 EndY=205 EndZ=0
    g27: LineSegment StartX=37.8518 StartY=206.716 StartZ=0 EndX=37.8518 EndY=233.284 EndZ=0
    g28: LineSegment StartX=36.1358 StartY=235 StartZ=0 EndX=29.5678 EndY=235 EndZ=0
    g29: ArcOfCircle CenterX=29.5678 CenterY=233.284 CenterZ=0 NormalX=0 NormalY=0 NormalZ=1 AngleXU=0 Radius=1.71599 StartAngle=1.5708 EndAngle=3.14159
    g30: GeomPoint X=24.6782 Y=236.929 Z=0
    g31: ArcOfCircle CenterX=36.1358 CenterY=233.284 CenterZ=0 NormalX=0 NormalY=0 NormalZ=1 AngleXU=0 Radius=1.71599 StartAngle=1.5e-15 EndAngle=1.5708
    g32: GeomPoint X=39.6782 Y=236.929 Z=0
    g33: ArcOfCircle CenterX=36.1358 CenterY=206.716 CenterZ=0 NormalX=0 NormalY=0 NormalZ=1 AngleXU=0 Radius=1.71599 StartAngle=4.71239 EndAngle=6.28319
    g34: GeomPoint X=39.6782 Y=201.929 Z=0
    g35: ArcOfCircle CenterX=29.5678 CenterY=206.716 CenterZ=0 NormalX=0 NormalY=0 NormalZ=1 AngleXU=0 Radius=1.71599 StartAngle=3.14159 EndAngle=4.71239
    g36: GeomPoint X=24.6782 Y=201.929 Z=0
    g37: LineSegment StartX=49 StartY=151 StartZ=0 EndX=110 EndY=151 EndZ=0
    g38: LineSegment StartX=110 StartY=151 StartZ=0 EndX=171 EndY=151 EndZ=0
    g39: LineSegment StartX=171 StartY=131 StartZ=0 EndX=171 EndY=116 EndZ=0
    g40: LineSegment StartX=171 StartY=116 StartZ=0 EndX=171 EndY=101 EndZ=0
    g41: LineSegment StartX=110 StartY=141.519 StartZ=0 EndX=63.9482 EndY=141.519 EndZ=0
    g42: LineSegment StartX=110 StartY=141.519 StartZ=0 EndX=154.396 EndY=141.519 EndZ=0
    g43: LineSegment StartX=159.951 StartY=135.965 StartZ=0 EndX=159.951 EndY=116 EndZ=0
    g44: LineSegment StartX=159.951 StartY=116 StartZ=0 EndX=159.951 EndY=96.3153 EndZ=0
    g45: LineSegment StartX=154.396 StartY=90.7606 StartZ=0 EndX=63.7857 EndY=90.7606 EndZ=0
    g46: LineSegment StartX=59.5711 StartY=94.9753 StartZ=0 EndX=59.5711 EndY=137.142 EndZ=0
    g47: ArcOfCircle CenterX=191.622 CenterY=230.131 CenterZ=0 NormalX=0 NormalY=0 NormalZ=1 AngleXU=0 Radius=0.786724 StartAngle=0.960036 EndAngle=1.92387
    g48: GeomPoint X=191.736 Y=231.012 Z=0
    g49: ArcOfCircle CenterX=192.415 CenterY=229.865 CenterZ=0 NormalX=0 NormalY=0 NormalZ=1 AngleXU=0 Radius=0.5505 StartAngle=6.28318 EndAngle=7.24322
    g50: GeomPoint X=192.965 Y=230.151 Z=0
    g51: ArcOfCircle CenterX=191.943 CenterY=211.298 CenterZ=0 NormalX=0 NormalY=0 NormalZ=1 AngleXU=0 Radius=1.02221 StartAngle=5.32325 EndAngle=6.28319
    g52: GeomPoint X=192.965 Y=210.766 Z=0
    g53: ArcOfCircle CenterX=191.617 CenterY=210.814 CenterZ=0 NormalX=0 NormalY=0 NormalZ=1 AngleXU=0 Radius=0.81238 StartAngle=4.36332 EndAngle=5.32325
    g54: GeomPoint X=191.736 Y=209.906 Z=0
    g55: ArcOfCircle CenterX=184.607 CenterY=213.803 CenterZ=0 NormalX=0 NormalY=0 NormalZ=1 AngleXU=0 Radius=1.2237 StartAngle=3.75245 EndAngle=4.36332
    g56: GeomPoint X=183.826 Y=212.785 Z=0
    g57: ArcOfCircle CenterX=184.706 CenterY=214.563 CenterZ=0 NormalX=0 NormalY=0 NormalZ=1 AngleXU=0 Radius=1.74122 StartAngle=3.14148 EndAngle=3.75245
    g58: GeomPoint X=182.965 Y=214.014 Z=0
    g59: ArcOfCircle CenterX=184.453 CenterY=226.432 CenterZ=0 NormalX=0 NormalY=0 NormalZ=1 AngleXU=0 Radius=1.4564 StartAngle=2.5473 EndAngle=3.13647
    g60: GeomPoint X=182.999 Y=226.881 Z=0
    g61: ArcOfCircle CenterX=184.616 CenterY=227.055 CenterZ=0 NormalX=0 NormalY=0 NormalZ=1 AngleXU=0 Radius=1.24259 StartAngle=1.92597 EndAngle=2.5473
    g62: GeomPoint X=183.81 Y=228.081 Z=0
    g63: ArcOfCircle CenterX=63.9482 CenterY=137.142 CenterZ=0 NormalX=0 NormalY=0 NormalZ=1 AngleXU=0 Radius=4.3771 StartAngle=1.5708 EndAngle=3.14159
    g64: GeomPoint X=59.5711 Y=141.519 Z=0
    g65: ArcOfCircle CenterX=63.7857 CenterY=94.9753 CenterZ=0 NormalX=0 NormalY=0 NormalZ=1 AngleXU=0 Radius=4.21464 StartAngle=3.14159 EndAngle=4.71239
    g66: GeomPoint X=59.5711 Y=90.7606 Z=0
    g67: ArcOfCircle CenterX=154.396 CenterY=96.3153 CenterZ=0 NormalX=0 NormalY=0 NormalZ=1 AngleXU=0 Radius=5.55461 StartAngle=4.71239 EndAngle=6.28319
    g68: GeomPoint X=159.951 Y=90.7606 Z=0
    g69: ArcOfCircle CenterX=154.396 CenterY=135.965 CenterZ=0 NormalX=0 NormalY=0 NormalZ=1 AngleXU=0 Radius=5.55461 StartAngle=-9e-16 EndAngle=1.5708
    g70: GeomPoint X=159.951 Y=141.519 Z=0
  constraints (90):
    c: Coincident(g25,g35)
    c: Coincident(g25,g29)
    c: Coincident(g26,g35)
    c: Coincident(g28,g29)
    c: Coincident(g26,g33)
    c: Coincident(g28,g31)
    c: Coincident(g27,g33)
    c: Coincident(g27,g31)
    c: Coincident(g41,g42)
    c: Coincident(g43,g44)
    c: Coincident(g9,g10)
    c: Coincident(g10,g11)
    c: Coincident(g7,g8)
    c: Coincident(g11,g12)
    c: Coincident(g3,g4)
    c: Coincident(g5,g6)
    c: Coincident(g6,g12)
    c: Vertical(g25)
    c: Vertical(g27)
    c: Horizontal(g26)
    c: Horizontal(g28)
    c: Equal(g29,g31)
    c: Equal(g31,g33)
    c: Equal(g33,g35)
    c: Vertical(g29,g35)
    c: Horizontal(g31,g29)
    c: Horizontal(g33,g35)
    c: DistanceX(g25,g27) = 10
    c: Horizontal(g26,g-7)
    c: Vertical(g26,g33)
    c: Horizontal(g27,g33)
    c: Horizontal(g31,g27)
    c: Horizontal(g29,g25)
    c: Vertical(g28,g29)
    c: Horizontal(g28,g-6)
    c: PointOnObject(g48,g4)
    c: PointOnObject(g48,g18)
    c: Tangent(g4,g47) = 1.5708
    c: Tangent(g18,g47) = -1.5708
    c: PointOnObject(g50,g18)
    c: PointOnObject(g50,g5)
    c: Tangent(g18,g49) = -1.5708
    c: Tangent(g5,g49) = 1.5708
    c: PointOnObject(g52,g6)
    c: PointOnObject(g52,g15)
    c: Tangent(g6,g51) = 1.5708
    c: Tangent(g15,g51) = -1.5708
    c: PointOnObject(g54,g15)
    c: PointOnObject(g54,g7)
    c: Tangent(g15,g53) = -1.5708
    c: Tangent(g7,g53) = 1.5708
    c: PointOnObject(g56,g8)
    c: PointOnObject(g56,g24)
    c: Tangent(g8,g55) = 1.5708
    c: Tangent(g24,g55) = -1.5708
    c: PointOnObject(g58,g24)
    c: PointOnObject(g58,g9)
    c: Tangent(g24,g57) = -1.5708
    c: Tangent(g9,g57) = 1.5708
    c: PointOnObject(g60,g10)
    c: PointOnObject(g60,g21)
    c: Tangent(g10,g59) = 1.5708
    c: Tangent(g21,g59) = -1.5708
    c: PointOnObject(g62,g21)
    c: PointOnObject(g62,g3)
    c: Tangent(g21,g61) = -1.5708
    c: Tangent(g3,g61) = 1.5708
    c: PointOnObject(g64,g46)
    c: PointOnObject(g64,g41)
    c: Tangent(g46,g63) = 1.5708
    c: Tangent(g41,g63) = -1.5708
    c: PointOnObject(g66,g46)
    c: PointOnObject(g66,g45)
    c: Tangent(g46,g65) = 1.5708
    c: Tangent(g45,g65) = 1.5708
    c: PointOnObject(g68,g45)
    c: PointOnObject(g68,g44)
    c: Tangent(g45,g67) = 1.5708
    c: Tangent(g44,g67) = 1.5708
    c: PointOnObject(g70,g43)
    c: PointOnObject(g70,g42)
    c: Tangent(g43,g69) = 1.5708
    c: Tangent(g42,g69) = 1.5708
    c: Vertical(g67,g69)
    c: Vertical(g43)
    c: Vertical(g44)
    c: Horizontal(g42)
    c: Horizontal(g41)
    c: Vertical(g46)
    c: Horizontal(g45)
FEATURE [Part::Part2DObjectPython] Clone2D001  label="Model-CUT-Functional"  # Draft 2D object (typed FeaturePython)
  Fuse = false
  Objects = -> [Sketch003]
  PathResource = Model
  Scale = (1,1,1)
FEATURE [Part::Part2DObjectPython] Clone2D002  label="Model-CUT-BOX-WALLS"  # Draft 2D object (typed FeaturePython)
  Fuse = false
  Objects = -> [Sketch004]
  PathResource = Model
  Scale = (1,1,1)
FEATURE [Part::Part2DObjectPython] Clone2D003  label="Model-CUT-BOX-WALS2"  # Draft 2D object (typed FeaturePython)
  Fuse = false
  Objects = -> [Sketch005]
  PathResource = Model
  Scale = (1,1,1)
FEATURE [Part::Part2DObjectPython] Clone2D004  label="Model-CUT-ROOF"  # Draft 2D object (typed FeaturePython)
  Fuse = false
  Objects = -> [Sketch006]
  PathResource = Model
  Scale = (1,1,1)
FEATURE [App::DocumentObjectGroup] Model
  Group = -> [Clone2D,Clone2D001,Clone2D002,Clone2D003,Clone2D004]
FEATURE [Path::FeaturePython] Job  # Path/CAM operation (typed FeaturePython)
  CycleTime = 00:00:03
  Fixtures = G54
  GeometryTolerance = 0.01
  Group = -> [Sketch005]
  JobType = 0
  Model = -> Model
  Operations = -> Operations
  OrderOutputBy = 0
  PostProcessor = 10
  PostProcessorOutputFile = <userpath>/Documents/AdruinoAtariPaddle/FREECAD/HousingAtari_RAW.nc
  SetupSheet = -> SetupSheet
  SplitOutput = false
  Stock = -> Stock001
  Tools = -> Tools
FEATURE [TechDraw::DrawSVGTemplate] Template
  Height = 210
  Orientation = 1
  Template = <path>
  Width = 297
FEATURE [TechDraw::DrawViewDraft] DraftView001
  Direction = (0,0,1)
  FontSize = 12
  LineSpacing = 1
  LineStyle = Solid
  LineWidth = 0.35
  LockPosition = false
  OverrideStyle = false
  Rotation = 0
  Scale = 0.6
  ScaleType = 2
  Source = -> Sketch006
  Symbol = <svg\n	xmlns="http://www.w3.org/2000/svg" version="1.1"\n	xmlns:freecad="http://www.freecad.org/wiki/index.php?title=Svg_Namespace">\n<g transform ="scale(1,-1)">\n    <path id="Sketch006_w0000"  d="M 49.0 151.0 L 49.0 131.0 L 45.0 131.0 L 45.0 101.0 L 49.0 101.0 L 49.0 81.0 L 83.7703438155425 81.0 L 83.7703438155425 77.0 L 133.7703438155425 77.00000000000001 L 133.7703438155425 81.00000000000001 L 171.0 81.00000000000001 L 171.0 101.00000000000001 L 175.0 101.00000000000001 L 175.0 131.0 L 171.0 131.0 L 171.0 151.0 " stroke="#000000" stroke-width="1.1666666666666667 px" style="stroke-width:1.1666666666666667;stroke-miterlimit:4;stroke-dasharray:none;stroke-linecap:square;fill:none;fill-opacity:1;fill-rule: evenodd"/>\n</g>\n\n</svg>
  X = 147.769
  Y = 49.2811
FEATURE [TechDraw::DrawViewDraft] DraftView002
  Direction = (0,0,1)
  FontSize = 12
  LineSpacing = 1
  LineStyle = Solid
  LineWidth = 0.35
  LockPosition = false
  OverrideStyle = false
  Rotation = 0
  Scale = 0.6
  ScaleType = 2
  Source = -> Sketch005
  Symbol = <svg\n	xmlns="http://www.w3.org/2000/svg" version="1.1"\n	xmlns:freecad="http://www.freecad.org/wiki/index.php?title=Svg_Namespace">\n<g transform ="scale(1,-1)">\n    <path id="Sketch005_w0000"  d="M 48.99999999999998 181.0 L 48.99999999999998 166.0 L 45.0 166.0 L 45.0 151.0 L 83.7703438155425 151.0 L 83.7703438155425 155.0 L 133.7703438155425 155.0 L 133.7703438155425 151.0 L 175.0 151.0 L 175.0 166.0 L 171.0 166.0 L 171.0 181.0 " stroke="#000000" stroke-width="1.1666666666666667 px" style="stroke-width:1.1666666666666667;stroke-miterlimit:4;stroke-dasharray:none;stroke-linecap:square;fill:none;fill-opacity:1;fill-rule: evenodd"/>\n<path id="Sketch005_w0001"  d="M 48.99999999999997 259.0 L 48.99999999999997 274.0 L 45.0 274.0 L 45.0 289.0 L 83.7703438155425 289.0 L 83.7703438155425 285.0 L 133.77034381554242 285.0 L 133.7703438155425 289.0 L 175.0 289.0 L 175.0 274.0 L 171.0 274.0 L 171.0 259.0 " stroke="#000000" stroke-width="1.1666666666666667 px" style="stroke-width:1.1666666666666667;stroke-miterlimit:4;stroke-dasharray:none;stroke-linecap:square;fill:none;fill-opacity:1;fill-rule: evenodd"/>\n</g>\n\n</svg>
  X = 147.769
  Y = 113.527
FEATURE [TechDraw::DrawViewDraft] DraftView003
  Direction = (0,0,1)
  FontSize = 12
  LineSpacing = 1
  LineStyle = Solid
  LineWidth = 0.35
  LockPosition = false
  OverrideStyle = false
  Rotation = 0
  Scale = 0.6
  ScaleType = 2
  Source = -> Sketch004
  Symbol = <svg\n	xmlns="http://www.w3.org/2000/svg" version="1.1"\n	xmlns:freecad="http://www.freecad.org/wiki/index.php?title=Svg_Namespace">\n<g transform ="scale(1,-1)">\n    <path id="Sketch004_w0000"  d="M 45.0 259.0 L 30.0 259.0 L 30.0 255.0 L 14.999999999999998 255.0 L 15.0 235.0 L 20.657879 235.0 L 20.657879 205.0 " stroke="#000000" stroke-width="1.1666666666666667 px" style="stroke-width:1.1666666666666667;stroke-miterlimit:4;stroke-dasharray:none;stroke-linecap:square;fill:none;fill-opacity:1;fill-rule: evenodd"/>\n<path id="Sketch004_w0001"  d="M 20.657879 204.687439 L 15.0 204.687439 L 15.0 185.0 L 30.0 185.0 L 30.0 181.0 L 45.0 181.0 " stroke="#000000" stroke-width="1.1666666666666667 px" style="stroke-width:1.1666666666666667;stroke-miterlimit:4;stroke-dasharray:none;stroke-linecap:square;fill:none;fill-opacity:1;fill-rule: evenodd"/>\n<path id="Sketch004_w0002"  d="M 175.0 181.0 L 190.0 181.0 L 190.0 185.0 L 205.0 185.0 L 205.0 205.0 L 199.0094149999999 205.0 L 199.0094149999999 235.0 L 205.0 234.99999999999974 L 205.0 255.0 L 190.0 255.0 L 190.0 259.0 L 175.0 259.0 " stroke="#000000" stroke-width="1.1666666666666667 px" style="stroke-width:1.1666666666666667;stroke-miterlimit:4;stroke-dasharray:none;stroke-linecap:square;fill:none;fill-opacity:1;fill-rule: evenodd"/>\n</g>\n\n</svg>
  X = 147.769
  Y = 114.014
FEATURE [TechDraw::DrawViewDraft] DraftView004
  Direction = (0,0,1)
  FontSize = 12
  LineSpacing = 1
  LineStyle = Solid
  LineWidth = 0.35
  LockPosition = false
  OverrideStyle = false
  Rotation = 0
  Scale = 0.6
  ScaleType = 2
  Source = -> Sketch002
  Symbol = <svg\n	xmlns="http://www.w3.org/2000/svg" version="1.1"\n	xmlns:freecad="http://www.freecad.org/wiki/index.php?title=Svg_Namespace">\n<g transform ="scale(1,-1)">\n    <path id="Sketch002_w0000"  d="M 45.0 181.0 L 83.7703438155425 181.0 L 83.7703438155425 185.00000000000003 L 110.0 185.0 L 133.7703438155425 185.0 L 133.7703438155425 181.0 L 175.0 181.0 L 175.0 205.0 L 171.0 205.0 L 171.0 220.0 L 171.0 235.0 L 175.0 235.0 L 175.0 259.0 L 133.7703438155425 259.0 L 133.7703438155425 255.0 L 110.0 255.0 L 83.7703438155425 255.0 L 83.7703438155425 259.0 L 45.0 259.0 L 45.0 235.0 L 49.0 235.0 L 49.0 220.0 L 49.0 205.0 L 45.0 205.0 L 45.0 181.0 " stroke="#000000" stroke-width="1.1666666666666667 px" style="stroke-width:1.1666666666666667;stroke-miterlimit:4;stroke-dasharray:none;stroke-linecap:square;fill:none;fill-opacity:1;fill-rule: evenodd"/>\n</g>\n\n</svg>
  X = 147.769
  Y = 114.014
FEATURE [TechDraw::DrawPage] Page
  KeepUpdated = true
  NextBalloonIndex = 1
  ProjectionType = 0
  Scale = 0.6
  Template = -> Template
  Views = -> [DraftView001,DraftView002,DraftView003,DraftView004]
note: 2 file-system paths scrubbed to <path> (originals preserved in the JSON sidecar)
